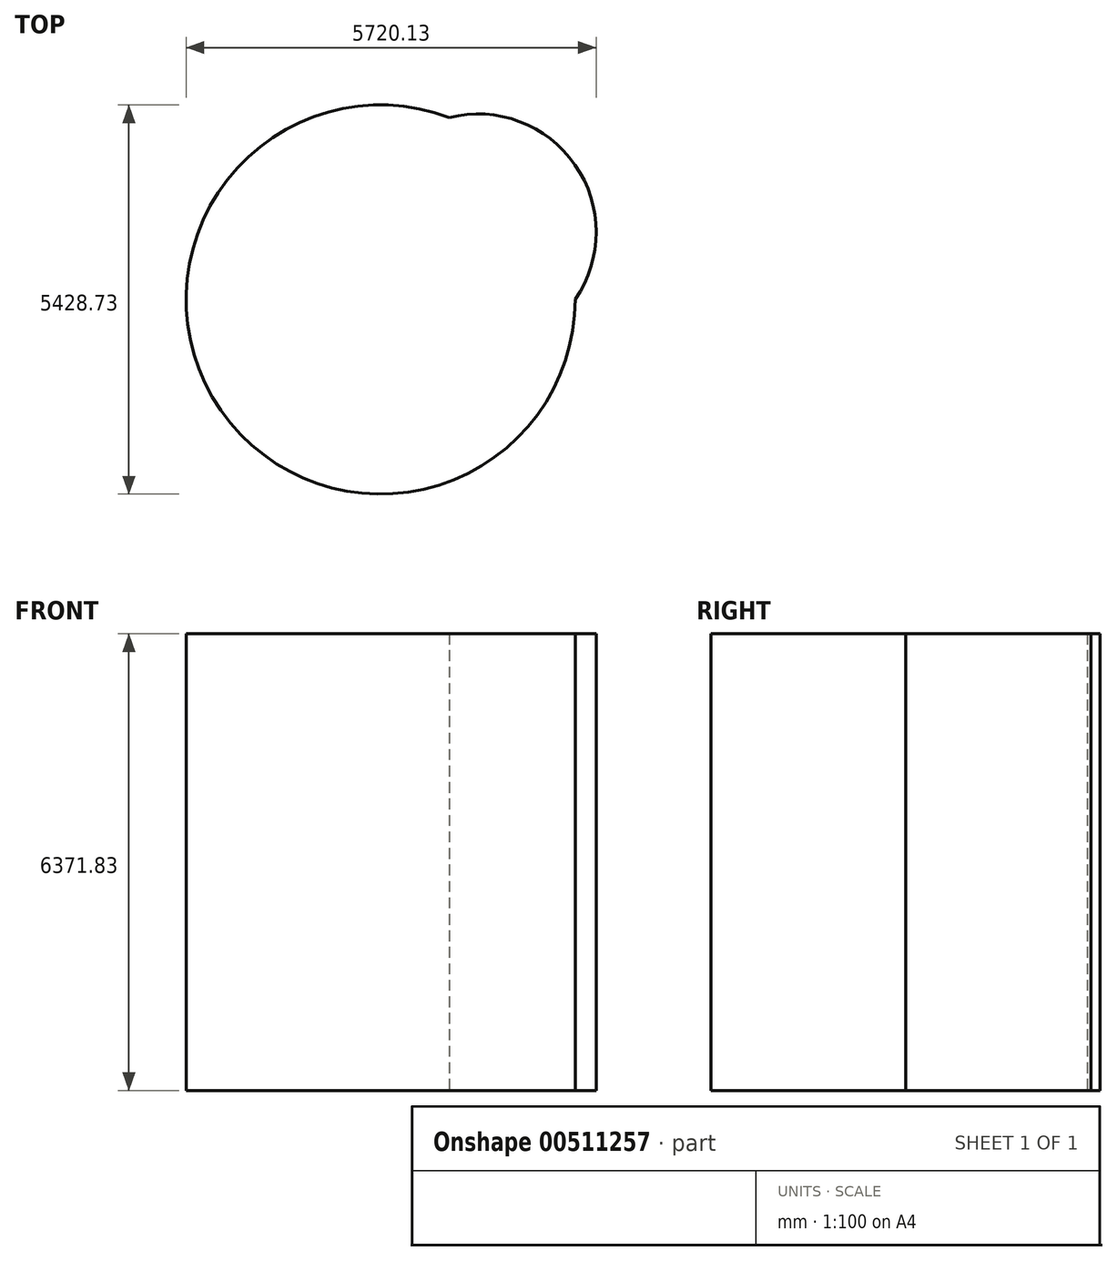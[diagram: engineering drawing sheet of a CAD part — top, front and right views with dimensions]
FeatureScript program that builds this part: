
annotation { "Feature Type Name" : "Feature", "Feature Type Description" : "" }
export const myFeature = defineFeature(function(context is Context, id is Id, definition is map)
    precondition{}
    {
        {
            var Q0;
            Q0=qCreatedBy(makeId("Top.planeOp"),FACE);
            var sketch = newSketch(context, id + "F0", { "sketchPlane" : qUnion([Q0])});
            skCircle(sketch, "E0", {"center": v(-92999.43, 1971.4) * mm, "radius": 46514.68 * mm});
            skCircle(sketch, "E1", {"center": v(-91540.77, 1924.45) * mm, "radius": 26840.42 * mm});
            skSolve(sketch);
        }
        {
            var Q0;
            Q0=makeQuery(id+"F0.imprint","IMPRINT",FACE,{"disambiguationData":[TD([[makeQuery(id+"F0.imprint","IMPRINT",EDGE,{"derivedFrom":sQuery(id+"F0.wireOp",EDGE,"E1")}),1.0]])]});
            var sketch = newSketch(context, id + "F1", { "sketchPlane" : qUnion([Q0])});
            skCircle(sketch, "E2", {"center": v(-118273.06, 0) * mm, "radius": 1649.66 * mm});
            skCircle(sketch, "E3", {"center": v(-119629.15, -939.35) * mm, "radius": 2714.36 * mm});
            skSolve(sketch);
        }
        {
            var Q0;
            Q0 = qSketchRegion(id + "F1", true);
            extrude(context, id + "F2", {"entities" : qUnion([Q0]), "depth" : 6371.83 * mm});
        }
    });
